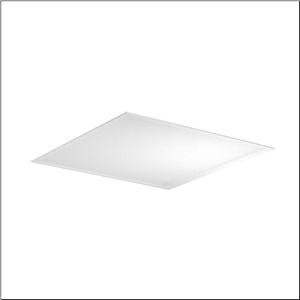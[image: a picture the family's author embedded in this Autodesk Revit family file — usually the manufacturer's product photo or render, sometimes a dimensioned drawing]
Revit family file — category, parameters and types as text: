
# Revit family: apollon_r__21_square_51mq12w72313_b113
name_source: partatom
category: Lighting Fixtures
units: mm (PartAtom-declared; Revit-internal decimal feet)

## family parameters
Cut with Voids When Loaded = No
Host = Face
Light Source = No
Part Type = Normal
Room Calculation Point = No
Round Connector Dimension = Use Diameter
Shared = No

## types (1)
- Apollon® 21 square (1 x LED, 4000 lm, 33 W, 3000K)
    Apparent Load = 33 VA
    CIE Flux Codes = 61 87 97 100 100
    Color Rendering = 80
    Color Temperature = 3000K
    Default Elevation = 1800 mm
    Description = Apollon® 21 square, office luminaire, primary optical cover: micro prismatic cover, of PMMA, CAT 2 (L<= 3000cd/m²), light emission: direct distribution, primary light characteristic: symmetric, installation type: lay-in mounting, LED, rated luminous flux: 4.000lm, luminous efficacy: 121lm/W, light colour: 830, colour temperature: 3000K, control gear: ECG, with terminal, 3-pole, mains connection: 220..240V, AC, 50/60Hz, rated input power: 33W, housing, of aluminium, traffic white (RAL 9016), module: M600, length: 596mm, width: 596mm, height: 40mm, housing upper side, of sheet steel, galvanised, protection rating (complete): IP20, protection rating (lamp compartment, on room side): IP50, insulation class (complete): insulation class II (safety insulation), certification: CE, ENEC, permissible operating ambient temperature: -20..+40°C, packaging unit: 1 piece
    Height = 0 mm  [stored 0 ft]
    Lamp = 1 x LED
    Lamp Light Flux = 4000 lm
    Lamp Power = 33 W
    Lamp count = 1
    Length = 595 mm
    Luminous efficacy = 121 lm/W
    Manufacturer = Siteco
    ModVariant = No
    Model = 51MQ12W72313
    Mounting Place = Ceiling
    Mounting Type = Recessed
    Number of Poles = 1
    OnlyDefault = Yes
    Power Factor = 1
    Product Name = Apollon® 21 square
    Product group = office luminaire | ceiling recessed
    ProductGroupID = 401
    Protection Class = Protection class II
    Protection Degree = IP 20
    RLX_Detail_Level = 1
    RLX_Emergency_Light_Flux = 0 lm
    RLX_Emergency_Type = 0
    RLX_Emergency_Type_DB = No
    RlxData = <blob elided: 14481 chars, md5=595a4ea8>
    Socket = socket
    Standby Power = 0 W
    System Light Flux = 4000 lm
    System Power = 33 W
    Type Comments = Product without accessories
    Type Image = l_1291049.jpg
    URL = http://relux.com
    VarID = ---
    Voltage = 0 V
    Weight = 0.00 kg
    Width = 595 mm

note: [stored X ft] marks values corroborated as IEEE doubles in the binary element streams (Revit-internal decimal feet)

## geometry (parser evidence)
native form markers: Sweep x11
no freeform markers — native parametric forms only
